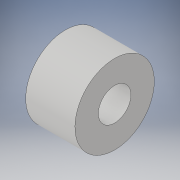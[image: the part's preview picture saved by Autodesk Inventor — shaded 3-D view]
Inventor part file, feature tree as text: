
AUTODESK INVENTOR PART (.ipt)
format: ipt  version: 2017 (Build 210142000, 142)  size: 95,232 bytes
history: native  units: in
note: dims shown in document units (in); Inventor stores cm internally (conversion verified against a paired STEP export)
features: extrude x1, sketch x1
ambient origin geometry x8: Origin, YZ Plane, XZ Plane, XY Plane, X Axis, Y Axis, Z Axis, Center Point
bodies: Solid1 (feature_tree)
feature tree (2):
  extrude  "Extrusion1"  Depth=0.378in
  sketch  "Sketch1"  dims[d0=0.609in d1=0.25in d2=0.378in d3=0.0in]
